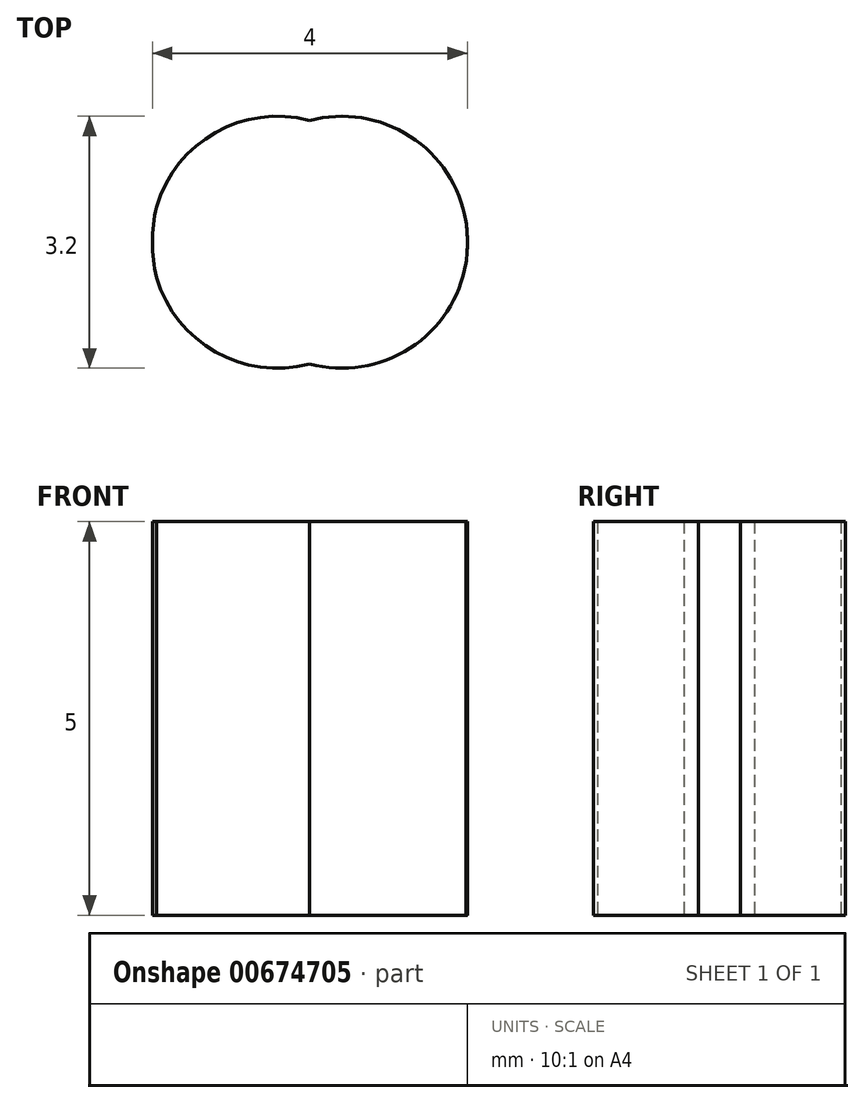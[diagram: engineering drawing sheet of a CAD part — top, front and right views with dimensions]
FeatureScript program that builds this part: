
annotation { "Feature Type Name" : "Feature", "Feature Type Description" : "" }
export const myFeature = defineFeature(function(context is Context, id is Id, definition is map)
    precondition{}
    {
        {
            var Q0;
            Q0=qCreatedBy(makeId("Top.planeOp"),FACE);
            var sketch = newSketch(context, id + "F0", { "sketchPlane" : qUnion([Q0])});
            skCircle(sketch, "E0", {"center": v(0, 0) * mm, "radius": 2 * mm});
            skCircle(sketch, "E1", {"center": v(-0.41, 0) * mm, "radius": 1.6 * mm});
            skCircle(sketch, "E2", {"center": v(0.4, 0) * mm, "radius": 1.6 * mm});
            skSolve(sketch);
        }
        {
            var Q0;
            {var subQ0=sQuery(id+"F0.wireOp",EDGE,"E1");var subQ1=sQuery(id+"F0.wireOp",EDGE,"E0");var subQ2=makeQuery(id+"F0.imprint","INTERSECT",VERTEX,{"disambiguationData":[OD(0.0)],"derivedFrom":[subQ1,subQ0]});Q0=makeQuery(id+"F0.imprint","IMPRINT",FACE,{"disambiguationData":[TD([[makeQuery(id+"F0.imprint","IMPRINT",EDGE,{"disambiguationData":[TD([[subQ2,-1.0]])],"derivedFrom":subQ1}),1.0]])]});}
            var Q1;
            {var subQ0=sQuery(id+"F0.wireOp",EDGE,"E2");var subQ1=sQuery(id+"F0.wireOp",EDGE,"E1");var subQ2=makeQuery(id+"F0.imprint","INTERSECT",VERTEX,{"disambiguationData":[OD(0.0)],"derivedFrom":[subQ1,subQ0]});Q1=makeQuery(id+"F0.imprint","IMPRINT",FACE,{"disambiguationData":[TD([[makeQuery(id+"F0.imprint","IMPRINT",EDGE,{"disambiguationData":[TD([[subQ2,1.0]])],"derivedFrom":subQ1}),1.0]])]});}
            var Q2;
            {var subQ0=sQuery(id+"F0.wireOp",EDGE,"E2");var subQ1=sQuery(id+"F0.wireOp",EDGE,"E0");var subQ2=makeQuery(id+"F0.imprint","INTERSECT",VERTEX,{"disambiguationData":[OD(0.0)],"derivedFrom":[subQ1,subQ0]});Q2=makeQuery(id+"F0.imprint","IMPRINT",FACE,{"disambiguationData":[TD([[makeQuery(id+"F0.imprint","IMPRINT",EDGE,{"disambiguationData":[TD([[subQ2,1.0]])],"derivedFrom":subQ1}),1.0]])]});}
            extrude(context, id + "F1", {"entities" : qUnion([Q0, Q1, Q2]), "depth" : 5 * mm, "offsetDistance" : 25 * mm});
        }
    });
